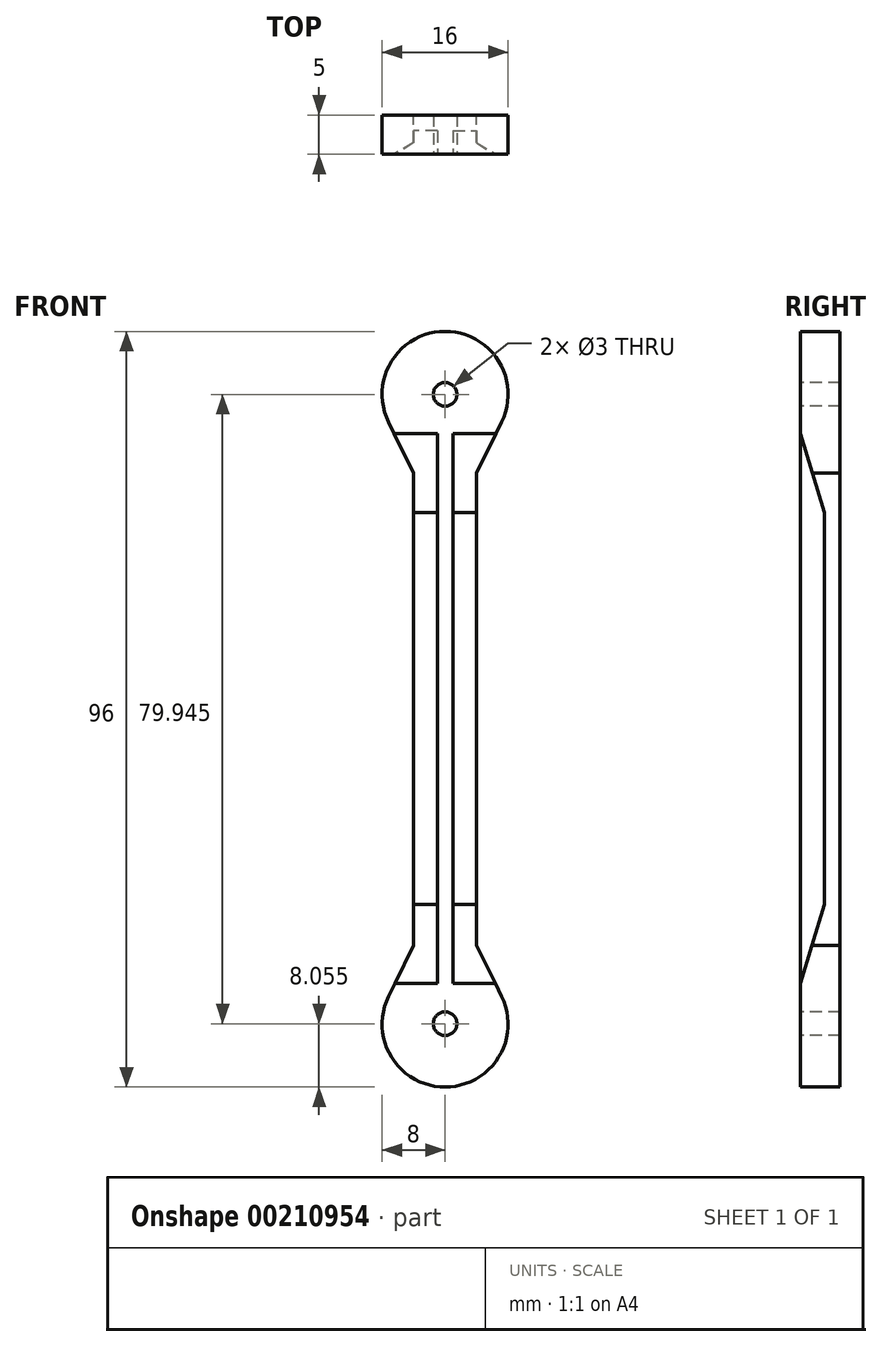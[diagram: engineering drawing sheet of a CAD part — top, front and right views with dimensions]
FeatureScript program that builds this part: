
annotation { "Feature Type Name" : "Feature", "Feature Type Description" : "" }
export const myFeature = defineFeature(function(context is Context, id is Id, definition is map)
    precondition{}
    {
        {
            var Q0;
            Q0=qCreatedBy(makeId("Front.planeOp"),FACE);
            var sketch = newSketch(context, id + "F0", { "sketchPlane" : qUnion([Q0])});
            skLineSegment(sketch, "E0", {"start": v(0, 0) * mm, "end": v(0, -80) * mm});
            skCircle(sketch, "E1", {"center": v(0, 0) * mm, "radius": 8 * mm});
            skCircle(sketch, "E2", {"center": v(0, -80) * mm, "radius": 8 * mm});
            skLineSegment(sketch, "E3", {"start": v(0, -15.1) * mm, "end": v(-4, -15.1) * mm});
            skLineSegment(sketch, "E4", {"start": v(-4, -15.1) * mm, "end": v(4, -15.1) * mm});
            skLineSegment(sketch, "E5", {"start": v(-4, -15.1) * mm, "end": v(-4, -73.07) * mm});
            skLineSegment(sketch, "E6", {"start": v(4, -15.1) * mm, "end": v(4, -6.93) * mm});
            skLineSegment(sketch, "E7", {"start": v(-4, -15.1) * mm, "end": v(-4, -6.93) * mm});
            skLineSegment(sketch, "E8", {"start": v(4, -15.1) * mm, "end": v(4, -73.07) * mm});
            skLineSegment(sketch, "E9", {"start": v(0, -80) * mm, "end": v(0, -70) * mm});
            skLineSegment(sketch, "E10", {"start": v(-4, -70) * mm, "end": v(-7.18, -76.47) * mm});
            skLineSegment(sketch, "E11", {"start": v(4, -70) * mm, "end": v(7.18, -76.47) * mm});
            skLineSegment(sketch, "E12", {"start": v(0, 0) * mm, "end": v(0, -10) * mm});
            skLineSegment(sketch, "E13", {"start": v(0, -10) * mm, "end": v(-4, -10) * mm});
            skPoint(sketch, "E13.endSnap0", {"position": v(-4, -11.02) * mm});
            skLineSegment(sketch, "E14", {"start": v(0, -10) * mm, "end": v(4, -10) * mm});
            skLineSegment(sketch, "E15", {"start": v(-4, -10) * mm, "end": v(-7.18, -3.53) * mm});
            skLineSegment(sketch, "E16", {"start": v(4, -10) * mm, "end": v(7.18, -3.53) * mm});
            skLineSegment(sketch, "E17", {"start": v(0, -80) * mm, "end": v(0, -65) * mm});
            skLineSegment(sketch, "E18", {"start": v(0, 0) * mm, "end": v(-1, 0) * mm});
            skLineSegment(sketch, "E19", {"start": v(0, 0) * mm, "end": v(1, 0) * mm});
            skSolve(sketch);
        }
        {
            var Q0;
            Q0 = qSketchRegion(id + "F0", true);
            extrude(context, id + "F1", {"entities" : qUnion([Q0]), "depth" : 5 * mm});
        }
        {
            var Q0;
            Q0=qCreatedBy(makeId("Right.planeOp"),FACE);
            cPlane(context, id + "F2", {"entities" : qUnion([Q0]), "cplaneType" : CPlaneType.OFFSET, "offset" : 10 * mm, "oppositeDirection" : true, "width" : 150 * mm, "height" : 150 * mm});
        }
        {
            var Q0;
            Q0=qCreatedBy(id+"F2.planeOp",FACE);
            var sketch = newSketch(context, id + "F3", { "sketchPlane" : qUnion([Q0])});
            skLineSegment(sketch, "E20", {"start": v(0, 0) * mm, "end": v(-2, 0) * mm});
            skLineSegment(sketch, "E21", {"start": v(-2, 0) * mm, "end": v(-2, -15) * mm});
            skLineSegment(sketch, "E22", {"start": v(-2, -15) * mm, "end": v(-5.4, -3.64) * mm});
            skLineSegment(sketch, "E23", {"start": v(-5.4, -3.64) * mm, "end": v(-5.4, -76.17) * mm});
            skLineSegment(sketch, "E24", {"start": v(-5.4, -76.17) * mm, "end": v(-2, -64.81) * mm});
            skLineSegment(sketch, "E25", {"start": v(-2, -64.81) * mm, "end": v(-2, -15) * mm});
            skSolve(sketch);
        }
        {
            var Q0;
            Q0=makeQuery(id+"F3.imprint","IMPRINT",FACE,{"disambiguationData":[TD([[makeQuery(id+"F3.imprint","IMPRINT",EDGE,{"derivedFrom":sQuery(id+"F3.wireOp",EDGE,"E22")}),1.0]])]});
            extrude(context, id + "F4", {"entities" : qUnion([Q0]), "operationType" : NewBodyOperationType.REMOVE, "depth" : 9 * mm});
        }
        {
            var Q0;
            Q0=makeQuery(id+"F1.opExtrude","CAP_FACE",FACE,{"disambiguationData":[OSD([sQuery(id+"F0.wireOp",EDGE,"E1"),sQuery(id+"F0.wireOp",EDGE,"E2"),sQuery(id+"F0.wireOp",EDGE,"E5"),sQuery(id+"F0.wireOp",EDGE,"E6"),sQuery(id+"F0.wireOp",EDGE,"E7"),sQuery(id+"F0.wireOp",EDGE,"E8"),sQuery(id+"F0.wireOp",EDGE,"E10"),sQuery(id+"F0.wireOp",EDGE,"E11"),sQuery(id+"F0.wireOp",EDGE,"E15"),sQuery(id+"F0.wireOp",EDGE,"E16")])],"isStart":false});
            var sketch = newSketch(context, id + "F5", { "sketchPlane" : qUnion([Q0])});
            skLineSegment(sketch, "E26", {"start": v(0, 0) * mm, "end": v(0, -80) * mm});
            skSolve(sketch);
        }
        {
            var Q0;
            Q0=qCreatedBy(makeId("Front.planeOp"),FACE);
            var sketch = newSketch(context, id + "F6", { "sketchPlane" : qUnion([Q0])});
            skLineSegment(sketch, "E27.bottom", {"start": v(0, 44.3) * mm, "end": v(44.08, 44.3) * mm});
            skLineSegment(sketch, "E27.top", {"start": v(0, -93.6) * mm, "end": v(44.08, -93.6) * mm});
            skLineSegment(sketch, "E27.left", {"start": v(0, 44.3) * mm, "end": v(0, -93.6) * mm});
            skLineSegment(sketch, "E27.right", {"start": v(44.08, 44.3) * mm, "end": v(44.08, -93.6) * mm});
            skSolve(sketch);
        }
        {
            var Q0;
            Q0 = qSketchRegion(id + "F6", true);
            extrude(context, id + "F7", {"entities" : qUnion([Q0]), "operationType" : NewBodyOperationType.REMOVE, "endBound" : BoundingType.SYMMETRIC, "oppositeDirection" : true, "depth" : 50 * mm});
        }
        {
            var Q0;
            Q0=makeQuery(id+"F1.opExtrude","SWEPT_BODY",BODY,{"disambiguationData":[OSD([sQuery(id+"F0.wireOp",EDGE,"E1"),sQuery(id+"F0.wireOp",EDGE,"E2"),sQuery(id+"F0.wireOp",EDGE,"E5"),sQuery(id+"F0.wireOp",EDGE,"E6"),sQuery(id+"F0.wireOp",EDGE,"E7"),sQuery(id+"F0.wireOp",EDGE,"E8"),sQuery(id+"F0.wireOp",EDGE,"E10"),sQuery(id+"F0.wireOp",EDGE,"E11"),sQuery(id+"F0.wireOp",EDGE,"E15"),sQuery(id+"F0.wireOp",EDGE,"E16")])]});
            var Q1;
            Q1=qCreatedBy(makeId("Right.planeOp"),FACE);
            mirror(context, id + "F8", {"operationType" : NewBodyOperationType.ADD, "entities" : qUnion([Q0]), "mirrorPlane" : qUnion([Q1])});
        }
        {
            var Q0;
            {var subQ8=sQuery(id+"F0.wireOp",EDGE,"E1");Q0=makeQuery(id+"F5.imprint","IMPRINT",FACE,{"disambiguationData":[TD([[makeQuery(id+"F5.imprint","IMPRINT",EDGE,{"derivedFrom":makeQuery(id+"F1.opExtrude","CAP_EDGE",EDGE,{"disambiguationData":[OSD([subQ8])],"isStart":false})}),1.0]])]});}
            var sketch = newSketch(context, id + "F9", { "sketchPlane" : qUnion([Q0])});
            skCircle(sketch, "E28", {"center": v(0, 0) * mm, "radius": 1.5 * mm});
            skCircle(sketch, "E29", {"center": v(0, -79.95) * mm, "radius": 1.5 * mm});
            skSolve(sketch);
        }
        {
            var Q0;
            Q0 = qSketchRegion(id + "F9", true);
            extrude(context, id + "F10", {"entities" : qUnion([Q0]), "operationType" : NewBodyOperationType.REMOVE, "oppositeDirection" : true, "depth" : 25 * mm});
        }
    });
